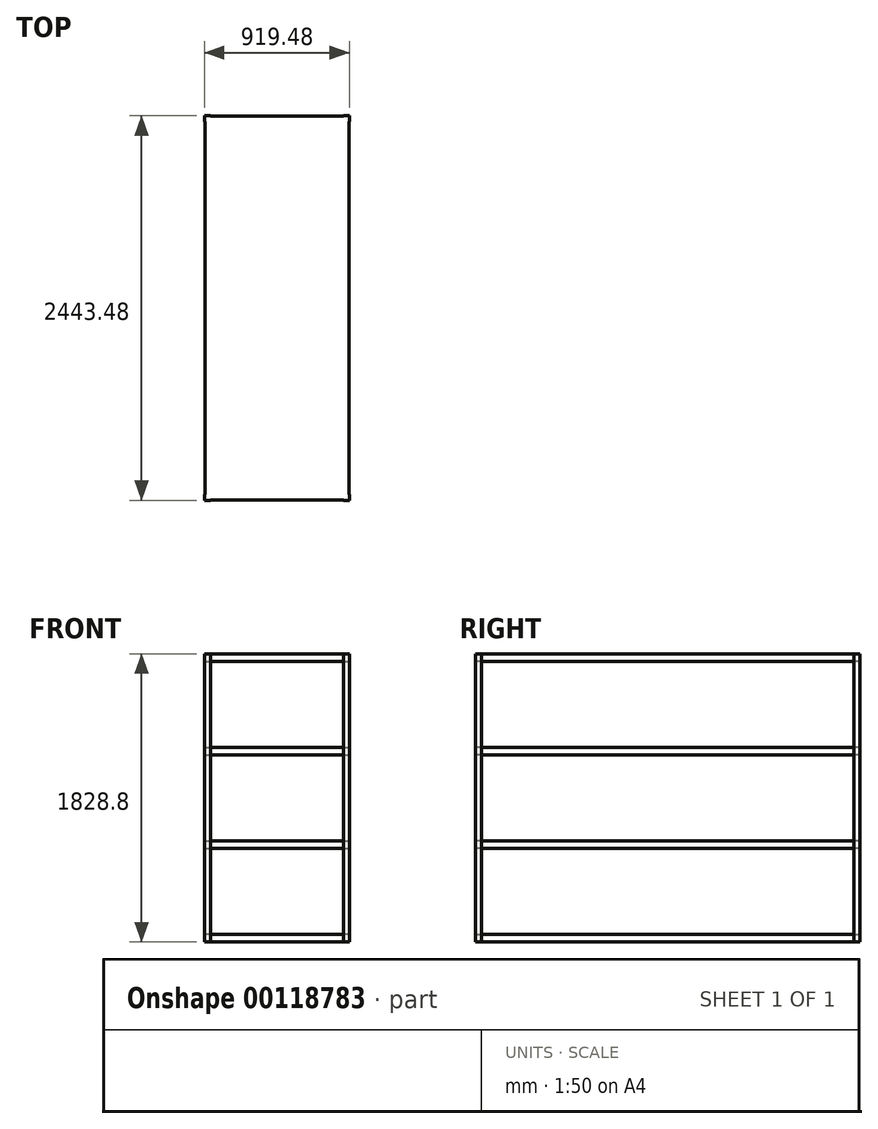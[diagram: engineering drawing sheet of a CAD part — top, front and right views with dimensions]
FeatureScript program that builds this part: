
annotation { "Feature Type Name" : "Feature", "Feature Type Description" : "" }
export const myFeature = defineFeature(function(context is Context, id is Id, definition is map)
    precondition{}
    {
        {
            var Q0;
            Q0=qCreatedBy(makeId("Top.planeOp"),FACE);
            var sketch = newSketch(context, id + "F0", { "sketchPlane" : qUnion([Q0])});
            skLineSegment(sketch, "E0.bottom", {"start": v(457.2, -1219.2) * mm, "end": v(-457.2, -1219.2) * mm});
            skLineSegment(sketch, "E0.top", {"start": v(457.2, 1219.2) * mm, "end": v(-457.2, 1219.2) * mm});
            skLineSegment(sketch, "E0.left", {"start": v(457.2, -1219.2) * mm, "end": v(457.2, 1219.2) * mm});
            skLineSegment(sketch, "E0.right", {"start": v(-457.2, -1219.2) * mm, "end": v(-457.2, 1219.2) * mm});
            skPoint(sketch, "E0.middle", {"position": v(0, 0) * mm});
            skSolve(sketch);
        }
        {
            var Q0;
            Q0 = qSketchRegion(id + "F0", true);
            extrude(context, id + "F1", {"entities" : qUnion([Q0]), "depth" : 47.62 * mm});
        }
        {
            var Q0;
            Q0=qCreatedBy(makeId("Top.planeOp"),FACE);
            var sketch = newSketch(context, id + "F2", { "sketchPlane" : qUnion([Q0])});
            skLineSegment(sketch, "E1.bottom", {"start": v(-459.74, 1221.74) * mm, "end": v(459.74, 1221.74) * mm});
            skLineSegment(sketch, "E1.top", {"start": v(-459.74, -1221.74) * mm, "end": v(459.74, -1221.74) * mm, "construction": true});
            skLineSegment(sketch, "E1.left", {"start": v(-459.74, 1221.74) * mm, "end": v(-459.74, -1221.74) * mm, "construction": true});
            skLineSegment(sketch, "E1.right", {"start": v(459.74, 1221.74) * mm, "end": v(459.74, -1221.74) * mm, "construction": true});
            skPoint(sketch, "E1.middle", {"position": v(0, 0) * mm});
            skLineSegment(sketch, "E2.bottom", {"start": v(-421.64, 1221.74) * mm, "end": v(-459.74, 1221.74) * mm, "construction": true});
            skLineSegment(sketch, "E2.top", {"start": v(-421.64, -1221.74) * mm, "end": v(-459.74, -1221.74) * mm, "construction": true});
            skLineSegment(sketch, "E2.left", {"start": v(-421.64, 1221.74) * mm, "end": v(-421.64, -1221.74) * mm, "construction": true});
            skLineSegment(sketch, "E3.bottom", {"start": v(-459.74, -1183.64) * mm, "end": v(459.74, -1183.64) * mm, "construction": true});
            skLineSegment(sketch, "E3.left", {"start": v(-459.74, -1183.64) * mm, "end": v(-459.74, -1221.74) * mm, "construction": true});
            skLineSegment(sketch, "E3.right", {"start": v(459.74, -1183.64) * mm, "end": v(459.74, -1221.74) * mm, "construction": true});
            skLineSegment(sketch, "E4.bottom", {"start": v(421.64, -1221.74) * mm, "end": v(459.74, -1221.74) * mm, "construction": true});
            skLineSegment(sketch, "E4.top", {"start": v(421.64, 1221.74) * mm, "end": v(459.74, 1221.74) * mm, "construction": true});
            skLineSegment(sketch, "E4.left", {"start": v(421.64, -1221.74) * mm, "end": v(421.64, 1221.74) * mm, "construction": true});
            skLineSegment(sketch, "E4.right", {"start": v(459.74, -1221.74) * mm, "end": v(459.74, 1221.74) * mm, "construction": true});
            skLineSegment(sketch, "E5.bottom", {"start": v(459.74, 1183.64) * mm, "end": v(-459.74, 1183.64) * mm, "construction": true});
            skLineSegment(sketch, "E5.top", {"start": v(459.74, 1221.74) * mm, "end": v(-459.74, 1221.74) * mm, "construction": true});
            skLineSegment(sketch, "E5.left", {"start": v(459.74, 1183.64) * mm, "end": v(459.74, 1221.74) * mm, "construction": true});
            skLineSegment(sketch, "E5.right", {"start": v(-459.74, 1183.64) * mm, "end": v(-459.74, 1221.74) * mm, "construction": true});
            skLineSegment(sketch, "E6", {"start": v(421.64, -1221.74) * mm, "end": v(421.64, -1219.2) * mm});
            skLineSegment(sketch, "E7", {"start": v(421.64, -1219.2) * mm, "end": v(457.2, -1219.2) * mm});
            skLineSegment(sketch, "E8", {"start": v(457.2, -1219.2) * mm, "end": v(457.2, -1183.64) * mm});
            skLineSegment(sketch, "E9", {"start": v(457.2, -1183.64) * mm, "end": v(459.74, -1183.64) * mm});
            skLineSegment(sketch, "E10", {"start": v(459.74, -1183.64) * mm, "end": v(459.74, -1221.74) * mm});
            skLineSegment(sketch, "E11", {"start": v(459.74, -1221.74) * mm, "end": v(421.64, -1221.74) * mm});
            skLineSegment(sketch, "E12", {"start": v(-459.74, -1183.64) * mm, "end": v(-459.74, -1221.74) * mm});
            skLineSegment(sketch, "E13", {"start": v(-459.74, -1183.64) * mm, "end": v(-457.2, -1183.64) * mm});
            skLineSegment(sketch, "E14", {"start": v(-457.2, -1183.64) * mm, "end": v(-457.2, -1219.2) * mm});
            skLineSegment(sketch, "E15", {"start": v(-457.2, -1219.2) * mm, "end": v(-421.64, -1219.2) * mm});
            skLineSegment(sketch, "E16", {"start": v(-421.64, -1219.2) * mm, "end": v(-421.64, -1221.74) * mm});
            skLineSegment(sketch, "E17", {"start": v(-421.64, -1221.74) * mm, "end": v(-459.74, -1221.74) * mm});
            skLineSegment(sketch, "E18", {"start": v(-459.74, 1183.64) * mm, "end": v(-457.2, 1183.64) * mm});
            skLineSegment(sketch, "E19", {"start": v(-457.2, 1183.64) * mm, "end": v(-457.2, 1219.2) * mm});
            skLineSegment(sketch, "E20", {"start": v(-457.2, 1219.2) * mm, "end": v(-421.64, 1219.2) * mm});
            skLineSegment(sketch, "E21", {"start": v(-421.64, 1219.2) * mm, "end": v(-421.64, 1221.74) * mm});
            skLineSegment(sketch, "E22", {"start": v(-459.74, 1221.74) * mm, "end": v(-421.64, 1221.74) * mm});
            skLineSegment(sketch, "E23", {"start": v(-459.74, 1221.74) * mm, "end": v(-459.74, 1183.64) * mm});
            skLineSegment(sketch, "E24", {"start": v(421.64, 1221.74) * mm, "end": v(459.74, 1221.74) * mm});
            skLineSegment(sketch, "E25", {"start": v(459.74, 1221.74) * mm, "end": v(459.74, 1183.64) * mm});
            skLineSegment(sketch, "E26", {"start": v(459.74, 1183.64) * mm, "end": v(457.2, 1183.64) * mm});
            skLineSegment(sketch, "E27", {"start": v(457.2, 1183.64) * mm, "end": v(457.2, 1219.2) * mm});
            skLineSegment(sketch, "E28", {"start": v(457.2, 1219.2) * mm, "end": v(421.64, 1219.2) * mm});
            skLineSegment(sketch, "E29", {"start": v(421.64, 1219.2) * mm, "end": v(421.64, 1221.74) * mm});
            skSolve(sketch);
        }
        {
            var Q0;
            Q0 = qSketchRegion(id + "F2", true);
            extrude(context, id + "F3", {"entities" : qUnion([Q0]), "operationType" : NewBodyOperationType.ADD, "depth" : 1828.8 * mm});
        }
        {
            var Q0;
            Q0=makeQuery(id+"F1.opExtrude","CAP_FACE",FACE,{"disambiguationData":[OSD([sQuery(id+"F0.wireOp",EDGE,"E0.bottom"),sQuery(id+"F0.wireOp",EDGE,"E0.top"),sQuery(id+"F0.wireOp",EDGE,"E0.left"),sQuery(id+"F0.wireOp",EDGE,"E0.right")])],"isStart":false});
            cPlane(context, id + "F4", {"entities" : qUnion([Q0]), "cplaneType" : CPlaneType.OFFSET, "offset" : 546.1 * mm, "width" : 152.4 * mm, "height" : 152.4 * mm});
        }
        {
            var Q0;
            Q0=qCreatedBy(id+"F4.planeOp",FACE);
            var sketch = newSketch(context, id + "F5", { "sketchPlane" : qUnion([Q0])});
            skLineSegment(sketch, "E30.bottom", {"start": v(-457.2, 1219.2) * mm, "end": v(457.2, 1219.2) * mm});
            skLineSegment(sketch, "E30.top", {"start": v(-457.2, -1219.2) * mm, "end": v(457.2, -1219.2) * mm});
            skLineSegment(sketch, "E30.left", {"start": v(-457.2, 1219.2) * mm, "end": v(-457.2, -1219.2) * mm});
            skLineSegment(sketch, "E30.right", {"start": v(457.2, 1219.2) * mm, "end": v(457.2, -1219.2) * mm});
            skPoint(sketch, "E30.middle", {"position": v(0, 0) * mm});
            skSolve(sketch);
        }
        {
            var Q0;
            Q0 = qSketchRegion(id + "F5", true);
            extrude(context, id + "F6", {"entities" : qUnion([Q0]), "operationType" : NewBodyOperationType.ADD, "depth" : 47.62 * mm});
        }
        {
            var Q0;
            Q0=makeQuery(id+"F6.opExtrude","CAP_FACE",FACE,{"disambiguationData":[OSD([sQuery(id+"F5.wireOp",EDGE,"E30.bottom"),sQuery(id+"F5.wireOp",EDGE,"E30.top"),sQuery(id+"F5.wireOp",EDGE,"E30.left"),sQuery(id+"F5.wireOp",EDGE,"E30.right")])],"isStart":false});
            cPlane(context, id + "F7", {"entities" : qUnion([Q0]), "cplaneType" : CPlaneType.OFFSET, "offset" : 546.1 * mm, "width" : 152.4 * mm, "height" : 152.4 * mm});
        }
        {
            var Q0;
            Q0=qCreatedBy(id+"F7.planeOp",FACE);
            var sketch = newSketch(context, id + "F8", { "sketchPlane" : qUnion([Q0])});
            skLineSegment(sketch, "E31.bottom", {"start": v(-457.2, 1219.2) * mm, "end": v(457.2, 1219.2) * mm});
            skLineSegment(sketch, "E31.top", {"start": v(-457.2, -1219.2) * mm, "end": v(457.2, -1219.2) * mm});
            skLineSegment(sketch, "E31.left", {"start": v(-457.2, 1219.2) * mm, "end": v(-457.2, -1219.2) * mm});
            skLineSegment(sketch, "E31.right", {"start": v(457.2, 1219.2) * mm, "end": v(457.2, -1219.2) * mm});
            skPoint(sketch, "E31.middle", {"position": v(0, 0) * mm});
            skSolve(sketch);
        }
        {
            var Q0;
            Q0 = qSketchRegion(id + "F8", true);
            extrude(context, id + "F9", {"entities" : qUnion([Q0]), "operationType" : NewBodyOperationType.ADD, "depth" : 47.62 * mm});
        }
        {
            var Q0;
            Q0=makeQuery(id+"F9.opExtrude","CAP_FACE",FACE,{"disambiguationData":[OSD([sQuery(id+"F8.wireOp",EDGE,"E31.bottom"),sQuery(id+"F8.wireOp",EDGE,"E31.top"),sQuery(id+"F8.wireOp",EDGE,"E31.left"),sQuery(id+"F8.wireOp",EDGE,"E31.right")])],"isStart":false});
            cPlane(context, id + "F10", {"entities" : qUnion([Q0]), "cplaneType" : CPlaneType.OFFSET, "offset" : 546.1 * mm, "width" : 152.4 * mm, "height" : 152.4 * mm});
        }
        {
            var Q0;
            Q0=qCreatedBy(id+"F10.planeOp",FACE);
            var sketch = newSketch(context, id + "F11", { "sketchPlane" : qUnion([Q0])});
            skLineSegment(sketch, "E32.bottom", {"start": v(-457.2, 1219.2) * mm, "end": v(457.2, 1219.2) * mm});
            skLineSegment(sketch, "E32.top", {"start": v(-457.2, -1219.2) * mm, "end": v(457.2, -1219.2) * mm});
            skLineSegment(sketch, "E32.left", {"start": v(-457.2, 1219.2) * mm, "end": v(-457.2, -1219.2) * mm});
            skLineSegment(sketch, "E32.right", {"start": v(457.2, 1219.2) * mm, "end": v(457.2, -1219.2) * mm});
            skPoint(sketch, "E32.middle", {"position": v(0, 0) * mm});
            skSolve(sketch);
        }
        {
            var Q0;
            Q0 = qSketchRegion(id + "F11", true);
            extrude(context, id + "F12", {"entities" : qUnion([Q0]), "operationType" : NewBodyOperationType.ADD, "depth" : 47.62 * mm});
        }
    });
